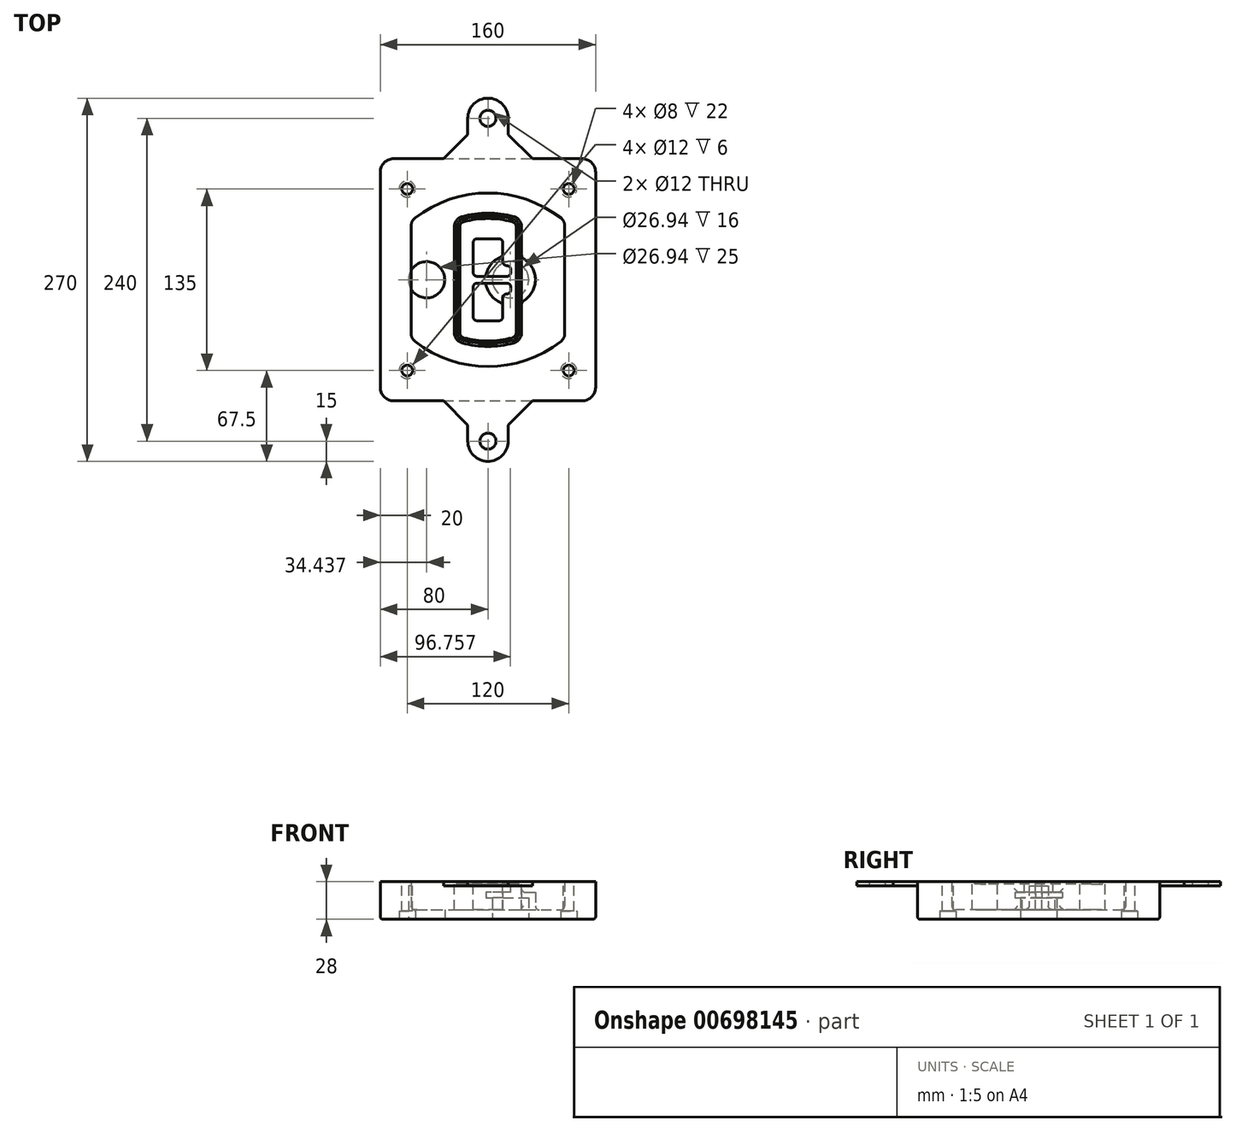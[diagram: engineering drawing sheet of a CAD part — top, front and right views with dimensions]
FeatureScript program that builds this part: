
annotation { "Feature Type Name" : "Feature", "Feature Type Description" : "" }
export const myFeature = defineFeature(function(context is Context, id is Id, definition is map)
    precondition{}
    {
        {
            var Q0;
            Q0=qCreatedBy(makeId("Top.planeOp"),FACE);
            var sketch = newSketch(context, id + "F0", { "sketchPlane" : qUnion([Q0])});
            skPoint(sketch, "E0.rect.middle", {"position": v(0, 0) * mm});
            skLineSegment(sketch, "E1.bottom", {"start": v(-70, -90) * mm, "end": v(70, -90) * mm});
            skLineSegment(sketch, "E1.top", {"start": v(-70, 90) * mm, "end": v(70, 90) * mm});
            skLineSegment(sketch, "E1.left", {"start": v(-80, -80) * mm, "end": v(-80, 80) * mm});
            skLineSegment(sketch, "E1.right", {"start": v(80, -80) * mm, "end": v(80, 80) * mm});
            skLineSegment(sketch, "E2", {"start": v(-80, 90) * mm, "end": v(80, -90) * mm, "construction": true});
            skLineSegment(sketch, "E3", {"start": v(80, 90) * mm, "end": v(-80, -90) * mm, "construction": true});
            skCircle(sketch, "E4", {"center": v(-60, 67.5) * mm, "radius": 4 * mm});
            skCircle(sketch, "E5", {"center": v(60, 67.5) * mm, "radius": 4 * mm});
            skCircle(sketch, "E6", {"center": v(60, -67.5) * mm, "radius": 4 * mm});
            skCircle(sketch, "E7", {"center": v(-60, -67.5) * mm, "radius": 4 * mm});
            skLineSegment(sketch, "E8", {"start": v(-60, 67.5) * mm, "end": v(60, 67.5) * mm, "construction": true});
            skLineSegment(sketch, "E9", {"start": v(60, 67.5) * mm, "end": v(60, -67.5) * mm, "construction": true});
            skLineSegment(sketch, "E10", {"start": v(60, -67.5) * mm, "end": v(-60, -67.5) * mm, "construction": true});
            skLineSegment(sketch, "E11", {"start": v(-60, -67.5) * mm, "end": v(-60, 67.5) * mm, "construction": true});
            skLineSegment(sketch, "E12", {"start": v(-60, 40.3) * mm, "end": v(-60, -40.3) * mm});
            skLineSegment(sketch, "E13", {"start": v(60, 40.3) * mm, "end": v(60, -40.3) * mm});
            skArc(sketch, "E14", {"start": v(56.15, 48.18) * mm, "mid": v(0, 67.5) * mm, "end": v(-56.15, 48.18) * mm});
            skArc(sketch, "E15", {"start": v(-56.15, -48.18) * mm, "mid": v(0, -67.5) * mm, "end": v(56.15, -48.18) * mm});
            skLineSegment(sketch, "E16", {"start": v(-60, 0) * mm, "end": v(60, 0) * mm, "construction": true});
            skPoint(sketch, "E17.visualSharp", {"position": v(-60, -45) * mm});
            skArc(sketch, "E17.filletArc", {"start": v(-60, -40.3) * mm, "mid": v(-58.99, -44.68) * mm, "end": v(-56.15, -48.18) * mm});
            skPoint(sketch, "E18.visualSharp", {"position": v(-60, 45) * mm});
            skArc(sketch, "E18.filletArc", {"start": v(-56.15, 48.18) * mm, "mid": v(-58.99, 44.68) * mm, "end": v(-60, 40.3) * mm});
            skPoint(sketch, "E19.visualSharp", {"position": v(60, 45) * mm});
            skArc(sketch, "E19.filletArc", {"start": v(60, 40.3) * mm, "mid": v(58.99, 44.68) * mm, "end": v(56.15, 48.18) * mm});
            skPoint(sketch, "E20.visualSharp", {"position": v(60, -45) * mm});
            skArc(sketch, "E20.filletArc", {"start": v(56.15, -48.18) * mm, "mid": v(58.99, -44.68) * mm, "end": v(60, -40.3) * mm});
            skPoint(sketch, "E21.visualSharp", {"position": v(-80, 90) * mm});
            skArc(sketch, "E21.filletArc", {"start": v(-70, 90) * mm, "mid": v(-77.07, 87.07) * mm, "end": v(-80, 80) * mm});
            skPoint(sketch, "E22.visualSharp", {"position": v(80, 90) * mm});
            skArc(sketch, "E22.filletArc", {"start": v(80, 80) * mm, "mid": v(77.07, 87.07) * mm, "end": v(70, 90) * mm});
            skPoint(sketch, "E23.visualSharp", {"position": v(80, -90) * mm});
            skArc(sketch, "E23.filletArc", {"start": v(70, -90) * mm, "mid": v(77.07, -87.07) * mm, "end": v(80, -80) * mm});
            skPoint(sketch, "E24.visualSharp", {"position": v(-80, -90) * mm});
            skArc(sketch, "E24.filletArc", {"start": v(-80, -80) * mm, "mid": v(-77.07, -87.07) * mm, "end": v(-70, -90) * mm});
            skArc(sketch, "E25.0", {"start": v(57, 40.3) * mm, "mid": v(56.3, 43.36) * mm, "end": v(54.3, 45.81) * mm});
            skLineSegment(sketch, "E25.1", {"start": v(57, 40.3) * mm, "end": v(57, -40.3) * mm});
            skArc(sketch, "E25.2", {"start": v(54.3, -45.81) * mm, "mid": v(56.3, -43.36) * mm, "end": v(57, -40.3) * mm});
            skArc(sketch, "E25.3", {"start": v(-54.3, -45.81) * mm, "mid": v(0, -64.5) * mm, "end": v(54.3, -45.81) * mm});
            skArc(sketch, "E25.4", {"start": v(-57, -40.3) * mm, "mid": v(-56.3, -43.36) * mm, "end": v(-54.3, -45.81) * mm});
            skArc(sketch, "E25.5", {"start": v(54.3, 45.81) * mm, "mid": v(0, 64.5) * mm, "end": v(-54.3, 45.81) * mm});
            skLineSegment(sketch, "E25.6", {"start": v(-57, 40.3) * mm, "end": v(-57, -40.3) * mm});
            skArc(sketch, "E25.7", {"start": v(-54.3, 45.81) * mm, "mid": v(-56.3, 43.36) * mm, "end": v(-57, 40.3) * mm});
            skArc(sketch, "E26.0", {"start": v(-58.62, 51.33) * mm, "mid": v(-62.58, 46.43) * mm, "end": v(-64, 40.3) * mm});
            skArc(sketch, "E26.1", {"start": v(58.62, 51.33) * mm, "mid": v(0, 71.5) * mm, "end": v(-58.62, 51.33) * mm});
            skArc(sketch, "E26.2", {"start": v(64, 40.3) * mm, "mid": v(62.58, 46.43) * mm, "end": v(58.62, 51.33) * mm});
            skLineSegment(sketch, "E26.3", {"start": v(64, 40.3) * mm, "end": v(64, -40.3) * mm});
            skArc(sketch, "E26.4", {"start": v(58.62, -51.33) * mm, "mid": v(62.58, -46.43) * mm, "end": v(64, -40.3) * mm});
            skLineSegment(sketch, "E26.5", {"start": v(-64, 40.3) * mm, "end": v(-64, -40.3) * mm});
            skArc(sketch, "E26.6", {"start": v(-58.62, -51.33) * mm, "mid": v(0, -71.5) * mm, "end": v(58.62, -51.33) * mm});
            skArc(sketch, "E26.7", {"start": v(-64, -40.3) * mm, "mid": v(-62.58, -46.43) * mm, "end": v(-58.62, -51.33) * mm});
            skSolve(sketch);
        }
        {
            var Q0;
            Q0=makeQuery(id+"F0.imprint","IMPRINT",FACE,{"disambiguationData":[TD([[makeQuery(id+"F0.imprint","IMPRINT",EDGE,{"derivedFrom":sQuery(id+"F0.wireOp",EDGE,"E1.bottom")}),1.0]])]});
            var Q1;
            Q1=makeQuery(id+"F0.imprint","IMPRINT",FACE,{"disambiguationData":[TD([[makeQuery(id+"F0.imprint","IMPRINT",EDGE,{"derivedFrom":sQuery(id+"F0.wireOp",EDGE,"E12")}),1.0]])]});
            var Q2;
            Q2=makeQuery(id+"F0.imprint","IMPRINT",FACE,{"disambiguationData":[TD([[makeQuery(id+"F0.imprint","IMPRINT",EDGE,{"derivedFrom":sQuery(id+"F0.wireOp",EDGE,"E25.0")}),1.0]])]});
            var Q3;
            Q3=makeQuery(id+"F0.imprint","IMPRINT",FACE,{"disambiguationData":[TD([[makeQuery(id+"F0.imprint","IMPRINT",EDGE,{"derivedFrom":sQuery(id+"F0.wireOp",EDGE,"E12")}),-1.0]])]});
            extrude(context, id + "F1", {"entities" : qUnion([Q0, Q1, Q2, Q3]), "oppositeDirection" : true, "depth" : 25 * mm});
        }
        {
            var Q0;
            Q0=makeQuery(id+"F0.imprint","IMPRINT",FACE,{"disambiguationData":[TD([[makeQuery(id+"F0.imprint","IMPRINT",EDGE,{"derivedFrom":sQuery(id+"F0.wireOp",EDGE,"E12")}),1.0]])]});
            extrude(context, id + "F2", {"entities" : qUnion([Q0]), "operationType" : NewBodyOperationType.ADD, "depth" : 3 * mm});
        }
        {
            var Q0;
            Q0=makeQuery(id+"F0.imprint","IMPRINT",FACE,{"disambiguationData":[TD([[makeQuery(id+"F0.imprint","IMPRINT",EDGE,{"derivedFrom":sQuery(id+"F0.wireOp",EDGE,"E25.0")}),1.0]])]});
            extrude(context, id + "F3", {"entities" : qUnion([Q0]), "operationType" : NewBodyOperationType.REMOVE, "oppositeDirection" : true, "depth" : 18 * mm});
        }
        {
            var Q0;
            Q0=makeQuery(id+"F2.opExtrude","CAP_FACE",FACE,{"disambiguationData":[OSD([sQuery(id+"F0.wireOp",EDGE,"E12"),sQuery(id+"F0.wireOp",EDGE,"E13"),sQuery(id+"F0.wireOp",EDGE,"E14"),sQuery(id+"F0.wireOp",EDGE,"E15"),sQuery(id+"F0.wireOp",EDGE,"E17.filletArc"),sQuery(id+"F0.wireOp",EDGE,"E18.filletArc"),sQuery(id+"F0.wireOp",EDGE,"E19.filletArc"),sQuery(id+"F0.wireOp",EDGE,"E20.filletArc"),sQuery(id+"F0.wireOp",EDGE,"E25.0"),sQuery(id+"F0.wireOp",EDGE,"E25.1"),sQuery(id+"F0.wireOp",EDGE,"E25.2"),sQuery(id+"F0.wireOp",EDGE,"E25.3"),sQuery(id+"F0.wireOp",EDGE,"E25.4"),sQuery(id+"F0.wireOp",EDGE,"E25.5"),sQuery(id+"F0.wireOp",EDGE,"E25.6"),sQuery(id+"F0.wireOp",EDGE,"E25.7")])],"isStart":false});
            var sketch = newSketch(context, id + "F4", { "sketchPlane" : qUnion([Q0])});
            skArc(sketch, "E27.0", {"start": v(-19.08, -46.97) * mm, "mid": v(0, -49.5) * mm, "end": v(19.08, -46.97) * mm});
            skArc(sketch, "E28.0", {"start": v(19.08, 46.97) * mm, "mid": v(0, 49.5) * mm, "end": v(-19.08, 46.97) * mm});
            skLineSegment(sketch, "E29", {"start": v(-25, 39.25) * mm, "end": v(-25, -39.25) * mm});
            skLineSegment(sketch, "E30", {"start": v(25, 39.25) * mm, "end": v(25, -39.25) * mm});
            skLineSegment(sketch, "E31", {"start": v(-25, 45.1) * mm, "end": v(25, 45.1) * mm, "construction": true});
            skLineSegment(sketch, "E32", {"start": v(-25, -45.1) * mm, "end": v(25, -45.1) * mm, "construction": true});
            skPoint(sketch, "E33.visualSharp", {"position": v(-25, 45.1) * mm});
            skArc(sketch, "E33.filletArc", {"start": v(-19.08, 46.97) * mm, "mid": v(-23.35, 44.11) * mm, "end": v(-25, 39.25) * mm});
            skPoint(sketch, "E34.visualSharp", {"position": v(25, 45.1) * mm});
            skArc(sketch, "E34.filletArc", {"start": v(25, 39.25) * mm, "mid": v(23.35, 44.11) * mm, "end": v(19.08, 46.97) * mm});
            skPoint(sketch, "E35.visualSharp", {"position": v(25, -45.1) * mm});
            skArc(sketch, "E35.filletArc", {"start": v(19.08, -46.97) * mm, "mid": v(23.35, -44.11) * mm, "end": v(25, -39.25) * mm});
            skPoint(sketch, "E36.visualSharp", {"position": v(-25, -45.1) * mm});
            skArc(sketch, "E36.filletArc", {"start": v(-25, -39.25) * mm, "mid": v(-23.35, -44.11) * mm, "end": v(-19.08, -46.97) * mm});
            skArc(sketch, "E37.0", {"start": v(54.3, 45.81) * mm, "mid": v(0, 64.5) * mm, "end": v(-54.3, 45.81) * mm});
            skArc(sketch, "E37.1", {"start": v(-54.3, 45.81) * mm, "mid": v(-56.3, 43.36) * mm, "end": v(-57, 40.3) * mm});
            skLineSegment(sketch, "E37.2", {"start": v(-57, 40.3) * mm, "end": v(-57, -40.3) * mm});
            skArc(sketch, "E37.3", {"start": v(-57, -40.3) * mm, "mid": v(-56.3, -43.36) * mm, "end": v(-54.3, -45.81) * mm});
            skArc(sketch, "E37.4", {"start": v(-54.3, -45.81) * mm, "mid": v(0, -64.5) * mm, "end": v(54.3, -45.81) * mm});
            skArc(sketch, "E37.5", {"start": v(54.3, -45.81) * mm, "mid": v(56.3, -43.36) * mm, "end": v(57, -40.3) * mm});
            skLineSegment(sketch, "E37.6", {"start": v(57, 40.3) * mm, "end": v(57, -40.3) * mm});
            skArc(sketch, "E37.7", {"start": v(57, 40.3) * mm, "mid": v(56.3, 43.36) * mm, "end": v(54.3, 45.81) * mm});
            skLineSegment(sketch, "E38.0", {"start": v(23, 39.25) * mm, "end": v(23, -39.25) * mm});
            skArc(sketch, "E38.1", {"start": v(18.56, -45.04) * mm, "mid": v(21.76, -42.9) * mm, "end": v(23, -39.25) * mm});
            skArc(sketch, "E38.2", {"start": v(-18.56, -45.04) * mm, "mid": v(0, -47.5) * mm, "end": v(18.56, -45.04) * mm});
            skArc(sketch, "E38.3", {"start": v(-23, -39.25) * mm, "mid": v(-21.76, -42.9) * mm, "end": v(-18.56, -45.04) * mm});
            skLineSegment(sketch, "E38.4", {"start": v(-23, 39.25) * mm, "end": v(-23, -39.25) * mm});
            skArc(sketch, "E38.5", {"start": v(23, 39.25) * mm, "mid": v(21.76, 42.9) * mm, "end": v(18.56, 45.04) * mm});
            skArc(sketch, "E38.6", {"start": v(-18.56, 45.04) * mm, "mid": v(-21.76, 42.9) * mm, "end": v(-23, 39.25) * mm});
            skArc(sketch, "E38.7", {"start": v(18.56, 45.04) * mm, "mid": v(0, 47.5) * mm, "end": v(-18.56, 45.04) * mm});
            skArc(sketch, "E39.0", {"start": v(21, 39.25) * mm, "mid": v(20.18, 41.68) * mm, "end": v(18.04, 43.1) * mm});
            skLineSegment(sketch, "E39.1", {"start": v(21, 39.25) * mm, "end": v(21, -39.25) * mm});
            skArc(sketch, "E39.2", {"start": v(18.04, -43.1) * mm, "mid": v(20.18, -41.68) * mm, "end": v(21, -39.25) * mm});
            skArc(sketch, "E39.3", {"start": v(-18.04, -43.1) * mm, "mid": v(0, -45.5) * mm, "end": v(18.04, -43.1) * mm});
            skArc(sketch, "E39.4", {"start": v(-21, -39.25) * mm, "mid": v(-20.18, -41.68) * mm, "end": v(-18.04, -43.1) * mm});
            skArc(sketch, "E39.5", {"start": v(18.04, 43.1) * mm, "mid": v(0, 45.5) * mm, "end": v(-18.04, 43.1) * mm});
            skLineSegment(sketch, "E39.6", {"start": v(-21, 39.25) * mm, "end": v(-21, -39.25) * mm});
            skArc(sketch, "E39.7", {"start": v(-18.04, 43.1) * mm, "mid": v(-20.18, 41.68) * mm, "end": v(-21, 39.25) * mm});
            skLineSegment(sketch, "E40", {"start": v(-25, 0) * mm, "end": v(25, 0) * mm, "construction": true});
            skLineSegment(sketch, "E41", {"start": v(-11, 5.5) * mm, "end": v(-11, 27.5) * mm});
            skLineSegment(sketch, "E42", {"start": v(-8, 30.5) * mm, "end": v(8, 30.5) * mm});
            skLineSegment(sketch, "E43", {"start": v(11, 27.5) * mm, "end": v(11, 13.5) * mm});
            skLineSegment(sketch, "E44", {"start": v(14, 10.5) * mm, "end": v(14, 10.5) * mm});
            skLineSegment(sketch, "E45", {"start": v(17, 7.5) * mm, "end": v(17, 5.5) * mm});
            skLineSegment(sketch, "E46", {"start": v(14, 2.5) * mm, "end": v(-8, 2.5) * mm});
            skPoint(sketch, "E47.visualSharp", {"position": v(-11, 30.5) * mm});
            skArc(sketch, "E47.filletArc", {"start": v(-8, 30.5) * mm, "mid": v(-10.12, 29.62) * mm, "end": v(-11, 27.5) * mm});
            skPoint(sketch, "E48.visualSharp", {"position": v(11, 30.5) * mm});
            skArc(sketch, "E48.filletArc", {"start": v(11, 27.5) * mm, "mid": v(10.12, 29.62) * mm, "end": v(8, 30.5) * mm});
            skPoint(sketch, "E49.visualSharp", {"position": v(11, 10.5) * mm});
            skArc(sketch, "E49.filletArc", {"start": v(11, 13.5) * mm, "mid": v(11.88, 11.38) * mm, "end": v(14, 10.5) * mm});
            skPoint(sketch, "E50.visualSharp", {"position": v(17, 10.5) * mm});
            skArc(sketch, "E50.filletArc", {"start": v(17, 7.5) * mm, "mid": v(16.12, 9.62) * mm, "end": v(14, 10.5) * mm});
            skPoint(sketch, "E51.visualSharp", {"position": v(17, 2.5) * mm});
            skArc(sketch, "E51.filletArc", {"start": v(14, 2.5) * mm, "mid": v(16.12, 3.38) * mm, "end": v(17, 5.5) * mm});
            skPoint(sketch, "E52.visualSharp", {"position": v(-11, 2.5) * mm});
            skArc(sketch, "E52.filletArc", {"start": v(-11, 5.5) * mm, "mid": v(-10.12, 3.38) * mm, "end": v(-8, 2.5) * mm});
            skLineSegment(sketch, "E53.0.MirrorCS", {"start": v(14, -2.5) * mm, "end": v(-8, -2.5) * mm});
            skArc(sketch, "E54.0.MirrorCS", {"start": v(-11, -5.5) * mm, "mid": v(-10.12, -3.38) * mm, "end": v(-8, -2.5) * mm});
            skLineSegment(sketch, "E55.0.MirrorCS", {"start": v(-11, -5.5) * mm, "end": v(-11, -27.5) * mm});
            skArc(sketch, "E56.0.MirrorCS", {"start": v(-8, -30.5) * mm, "mid": v(-10.12, -29.62) * mm, "end": v(-11, -27.5) * mm});
            skLineSegment(sketch, "E57.0.MirrorCS", {"start": v(-8, -30.5) * mm, "end": v(8, -30.5) * mm});
            skArc(sketch, "E58.0.MirrorCS", {"start": v(11, -27.5) * mm, "mid": v(10.12, -29.62) * mm, "end": v(8, -30.5) * mm});
            skLineSegment(sketch, "E59.0.MirrorCS", {"start": v(11, -27.5) * mm, "end": v(11, -13.5) * mm});
            skArc(sketch, "E60.0.MirrorCS", {"start": v(11, -13.5) * mm, "mid": v(11.88, -11.38) * mm, "end": v(14, -10.5) * mm});
            skArc(sketch, "E61.0.MirrorCS", {"start": v(17, -7.5) * mm, "mid": v(16.12, -9.62) * mm, "end": v(14, -10.5) * mm});
            skLineSegment(sketch, "E62.0.MirrorCS", {"start": v(17, -7.5) * mm, "end": v(17, -5.5) * mm});
            skArc(sketch, "E63.0.MirrorCS", {"start": v(14, -2.5) * mm, "mid": v(16.12, -3.38) * mm, "end": v(17, -5.5) * mm});
            skSolve(sketch);
        }
        {
            var Q0;
            Q0=makeQuery(id+"F4.imprint","IMPRINT",FACE,{"disambiguationData":[TD([[makeQuery(id+"F4.imprint","IMPRINT",EDGE,{"derivedFrom":sQuery(id+"F4.wireOp",EDGE,"E27.0")}),1.0]])]});
            var Q1;
            Q1=makeQuery(id+"F4.imprint","IMPRINT",FACE,{"disambiguationData":[TD([[makeQuery(id+"F4.imprint","IMPRINT",EDGE,{"derivedFrom":sQuery(id+"F4.wireOp",EDGE,"E38.0")}),-1.0]])]});
            var Q2;
            Q2=makeQuery(id+"F4.imprint","IMPRINT",FACE,{"disambiguationData":[TD([[makeQuery(id+"F4.imprint","IMPRINT",EDGE,{"derivedFrom":sQuery(id+"F4.wireOp",EDGE,"E39.0")}),1.0]])]});
            extrude(context, id + "F5", {"entities" : qUnion([Q0, Q1, Q2]), "operationType" : NewBodyOperationType.ADD, "endBound" : BoundingType.UP_TO_NEXT, "oppositeDirection" : true, "depth" : 25 * mm});
        }
        {
            var Q0;
            Q0=makeQuery(id+"F4.imprint","IMPRINT",FACE,{"disambiguationData":[TD([[makeQuery(id+"F4.imprint","IMPRINT",EDGE,{"derivedFrom":sQuery(id+"F4.wireOp",EDGE,"E38.0")}),-1.0]])]});
            extrude(context, id + "F6", {"entities" : qUnion([Q0]), "operationType" : NewBodyOperationType.REMOVE, "oppositeDirection" : true, "depth" : 2 * mm});
        }
        {
            var Q0;
            Q0=makeQuery(id+"F1.opExtrude","CAP_FACE",FACE,{"disambiguationData":[OSD([sQuery(id+"F0.wireOp",EDGE,"E1.bottom"),sQuery(id+"F0.wireOp",EDGE,"E1.top"),sQuery(id+"F0.wireOp",EDGE,"E1.left"),sQuery(id+"F0.wireOp",EDGE,"E1.right"),sQuery(id+"F0.wireOp",EDGE,"E4"),sQuery(id+"F0.wireOp",EDGE,"E5"),sQuery(id+"F0.wireOp",EDGE,"E6"),sQuery(id+"F0.wireOp",EDGE,"E7"),sQuery(id+"F0.wireOp",EDGE,"E21.filletArc"),sQuery(id+"F0.wireOp",EDGE,"E22.filletArc"),sQuery(id+"F0.wireOp",EDGE,"E23.filletArc"),sQuery(id+"F0.wireOp",EDGE,"E24.filletArc")])],"isStart":false});
            var sketch = newSketch(context, id + "F7", { "sketchPlane" : qUnion([Q0])});
            skCircle(sketch, "E64", {"center": v(16.76, 0) * mm, "radius": 13.47 * mm});
            skCircle(sketch, "E65", {"center": v(-45.56, 0) * mm, "radius": 13.47 * mm});
            skLineSegment(sketch, "E66", {"start": v(80, 0) * mm, "end": v(-80, 0) * mm});
            skCircle(sketch, "E67", {"center": v(16.76, 0) * mm, "radius": 18.47 * mm});
            skCircle(sketch, "E68", {"center": v(60, -67.5) * mm, "radius": 6 * mm});
            skCircle(sketch, "E69", {"center": v(-60, -67.5) * mm, "radius": 6 * mm});
            skCircle(sketch, "E70", {"center": v(-60, 67.5) * mm, "radius": 6 * mm});
            skCircle(sketch, "E71", {"center": v(60, 67.5) * mm, "radius": 6 * mm});
            skSolve(sketch);
        }
        {
            var Q0;
            {var subQ1=sQuery(id+"F7.wireOp",EDGE,"E66");var subQ4=sQuery(id+"F7.wireOp",EDGE,"E64");var subQ6=makeQuery(id+"F7.imprint","INTERSECT",VERTEX,{"disambiguationData":[OD(0.0)],"derivedFrom":[subQ4,subQ1]});Q0=makeQuery(id+"F7.imprint","IMPRINT",FACE,{"disambiguationData":[TD([[makeQuery(id+"F7.imprint","IMPRINT",EDGE,{"disambiguationData":[TD([[subQ6,-1.0]])],"derivedFrom":subQ4}),-1.0]])]});}
            var Q1;
            {var subQ0=sQuery(id+"F7.wireOp",EDGE,"E66");var subQ1=sQuery(id+"F7.wireOp",EDGE,"E64");var subQ3=makeQuery(id+"F7.imprint","INTERSECT",VERTEX,{"disambiguationData":[OD(0.0)],"derivedFrom":[subQ1,subQ0]});Q1=makeQuery(id+"F7.imprint","IMPRINT",FACE,{"disambiguationData":[TD([[makeQuery(id+"F7.imprint","IMPRINT",EDGE,{"disambiguationData":[TD([[subQ3,-1.0]])],"derivedFrom":subQ1}),1.0]])]});}
            var Q2;
            {var subQ0=sQuery(id+"F7.wireOp",EDGE,"E66");var subQ1=sQuery(id+"F7.wireOp",EDGE,"E64");var subQ3=makeQuery(id+"F7.imprint","INTERSECT",VERTEX,{"disambiguationData":[OD(0.0)],"derivedFrom":[subQ1,subQ0]});Q2=makeQuery(id+"F7.imprint","IMPRINT",FACE,{"disambiguationData":[TD([[makeQuery(id+"F7.imprint","IMPRINT",EDGE,{"disambiguationData":[TD([[subQ3,1.0]])],"derivedFrom":subQ1}),1.0]])]});}
            var Q3;
            {var subQ1=sQuery(id+"F7.wireOp",EDGE,"E66");var subQ4=sQuery(id+"F7.wireOp",EDGE,"E64");var subQ6=makeQuery(id+"F7.imprint","INTERSECT",VERTEX,{"disambiguationData":[OD(0.0)],"derivedFrom":[subQ4,subQ1]});Q3=makeQuery(id+"F7.imprint","IMPRINT",FACE,{"disambiguationData":[TD([[makeQuery(id+"F7.imprint","IMPRINT",EDGE,{"disambiguationData":[TD([[subQ6,1.0]])],"derivedFrom":subQ4}),-1.0]])]});}
            extrude(context, id + "F8", {"entities" : qUnion([Q0, Q1, Q2, Q3]), "operationType" : NewBodyOperationType.ADD, "oppositeDirection" : true, "depth" : 20 * mm});
        }
        {
            var Q0;
            {var subQ0=sQuery(id+"F7.wireOp",EDGE,"E66");var subQ1=sQuery(id+"F7.wireOp",EDGE,"E64");var subQ3=makeQuery(id+"F7.imprint","INTERSECT",VERTEX,{"disambiguationData":[OD(0.0)],"derivedFrom":[subQ1,subQ0]});Q0=makeQuery(id+"F7.imprint","IMPRINT",FACE,{"disambiguationData":[TD([[makeQuery(id+"F7.imprint","IMPRINT",EDGE,{"disambiguationData":[TD([[subQ3,-1.0]])],"derivedFrom":subQ1}),1.0]])]});}
            var Q1;
            {var subQ0=sQuery(id+"F7.wireOp",EDGE,"E66");var subQ1=sQuery(id+"F7.wireOp",EDGE,"E64");var subQ3=makeQuery(id+"F7.imprint","INTERSECT",VERTEX,{"disambiguationData":[OD(0.0)],"derivedFrom":[subQ1,subQ0]});Q1=makeQuery(id+"F7.imprint","IMPRINT",FACE,{"disambiguationData":[TD([[makeQuery(id+"F7.imprint","IMPRINT",EDGE,{"disambiguationData":[TD([[subQ3,1.0]])],"derivedFrom":subQ1}),1.0]])]});}
            extrude(context, id + "F9", {"entities" : qUnion([Q0, Q1]), "operationType" : NewBodyOperationType.REMOVE, "oppositeDirection" : true, "depth" : 16 * mm});
        }
        {
            var Q0;
            {var subQ0=sQuery(id+"F7.wireOp",EDGE,"E66");var subQ1=sQuery(id+"F7.wireOp",EDGE,"E65");var subQ3=makeQuery(id+"F7.imprint","INTERSECT",VERTEX,{"disambiguationData":[OD(0.0)],"derivedFrom":[subQ1,subQ0]});Q0=makeQuery(id+"F7.imprint","IMPRINT",FACE,{"disambiguationData":[TD([[makeQuery(id+"F7.imprint","IMPRINT",EDGE,{"disambiguationData":[TD([[subQ3,-1.0]])],"derivedFrom":subQ1}),1.0]])]});}
            var Q1;
            {var subQ0=sQuery(id+"F7.wireOp",EDGE,"E66");var subQ1=sQuery(id+"F7.wireOp",EDGE,"E65");var subQ3=makeQuery(id+"F7.imprint","INTERSECT",VERTEX,{"disambiguationData":[OD(0.0)],"derivedFrom":[subQ1,subQ0]});Q1=makeQuery(id+"F7.imprint","IMPRINT",FACE,{"disambiguationData":[TD([[makeQuery(id+"F7.imprint","IMPRINT",EDGE,{"disambiguationData":[TD([[subQ3,1.0]])],"derivedFrom":subQ1}),1.0]])]});}
            extrude(context, id + "F10", {"entities" : qUnion([Q0, Q1]), "operationType" : NewBodyOperationType.REMOVE, "oppositeDirection" : true, "depth" : 25 * mm});
        }
        {
            var Q0;
            Q0=makeQuery(id+"F7.imprint","IMPRINT",FACE,{"disambiguationData":[TD([[makeQuery(id+"F7.imprint","IMPRINT",EDGE,{"derivedFrom":sQuery(id+"F7.wireOp",EDGE,"E68")}),1.0]])]});
            var Q1;
            Q1=makeQuery(id+"F7.imprint","IMPRINT",FACE,{"disambiguationData":[TD([[makeQuery(id+"F7.imprint","IMPRINT",EDGE,{"derivedFrom":makeQuery(id+"F1.opExtrude","CAP_EDGE",EDGE,{"disambiguationData":[OSD([sQuery(id+"F0.wireOp",EDGE,"E5")])],"isStart":false})}),-1.0]])]});
            var Q2;
            Q2=makeQuery(id+"F7.imprint","IMPRINT",FACE,{"disambiguationData":[TD([[makeQuery(id+"F7.imprint","IMPRINT",EDGE,{"derivedFrom":sQuery(id+"F7.wireOp",EDGE,"E69")}),1.0]])]});
            var Q3;
            Q3=makeQuery(id+"F7.imprint","IMPRINT",FACE,{"disambiguationData":[TD([[makeQuery(id+"F7.imprint","IMPRINT",EDGE,{"derivedFrom":makeQuery(id+"F1.opExtrude","CAP_EDGE",EDGE,{"disambiguationData":[OSD([sQuery(id+"F0.wireOp",EDGE,"E4")])],"isStart":false})}),-1.0]])]});
            var Q4;
            Q4=makeQuery(id+"F7.imprint","IMPRINT",FACE,{"disambiguationData":[TD([[makeQuery(id+"F7.imprint","IMPRINT",EDGE,{"derivedFrom":sQuery(id+"F7.wireOp",EDGE,"E70")}),1.0]])]});
            var Q5;
            Q5=makeQuery(id+"F7.imprint","IMPRINT",FACE,{"disambiguationData":[TD([[makeQuery(id+"F7.imprint","IMPRINT",EDGE,{"derivedFrom":makeQuery(id+"F1.opExtrude","CAP_EDGE",EDGE,{"disambiguationData":[OSD([sQuery(id+"F0.wireOp",EDGE,"E7")])],"isStart":false})}),-1.0]])]});
            var Q6;
            Q6=makeQuery(id+"F7.imprint","IMPRINT",FACE,{"disambiguationData":[TD([[makeQuery(id+"F7.imprint","IMPRINT",EDGE,{"derivedFrom":sQuery(id+"F7.wireOp",EDGE,"E71")}),1.0]])]});
            var Q7;
            Q7=makeQuery(id+"F7.imprint","IMPRINT",FACE,{"disambiguationData":[TD([[makeQuery(id+"F7.imprint","IMPRINT",EDGE,{"derivedFrom":makeQuery(id+"F1.opExtrude","CAP_EDGE",EDGE,{"disambiguationData":[OSD([sQuery(id+"F0.wireOp",EDGE,"E6")])],"isStart":false})}),-1.0]])]});
            extrude(context, id + "F11", {"entities" : qUnion([Q0, Q1, Q2, Q3, Q4, Q5, Q6, Q7]), "operationType" : NewBodyOperationType.REMOVE, "oppositeDirection" : true, "depth" : 6 * mm});
        }
        {
            var Q0;
            Q0=makeQuery(id+"F9.boolean.opBoolean","COPY",FACE,{"derivedFrom":makeQuery(id+"F9.opExtrude","CAP_FACE",FACE,{"disambiguationData":[OSD([sQuery(id+"F7.wireOp",EDGE,"E64")])],"isStart":false})});
            var sketch = newSketch(context, id + "F12", { "sketchPlane" : qUnion([Q0])});
            skArc(sketch, "E72.0", {"start": v(11, 17.55) * mm, "mid": v(2.57, 11.82) * mm, "end": v(-1.54, 2.5) * mm});
            skArc(sketch, "E72.1", {"start": v(-1.54, -2.5) * mm, "mid": v(2.57, -11.82) * mm, "end": v(11, -17.55) * mm});
            skLineSegment(sketch, "E73", {"start": v(-1.54, -2.5) * mm, "end": v(14, -2.5) * mm});
            skLineSegment(sketch, "E74.0", {"start": v(14, 2.5) * mm, "end": v(-1.54, 2.5) * mm});
            skArc(sketch, "E74.1", {"start": v(14, 2.5) * mm, "mid": v(16.12, 3.38) * mm, "end": v(17, 5.5) * mm});
            skLineSegment(sketch, "E74.2", {"start": v(17, 7.5) * mm, "end": v(17, 5.5) * mm});
            skArc(sketch, "E74.3", {"start": v(17, 7.5) * mm, "mid": v(16.12, 9.62) * mm, "end": v(14, 10.5) * mm});
            skArc(sketch, "E74.4", {"start": v(11, 13.5) * mm, "mid": v(11.88, 11.38) * mm, "end": v(14, 10.5) * mm});
            skLineSegment(sketch, "E74.5", {"start": v(11, 17.55) * mm, "end": v(11, 13.5) * mm});
            skLineSegment(sketch, "E74.7", {"start": v(14, -2.5) * mm, "end": v(-1.54, -2.5) * mm});
            skArc(sketch, "E74.8", {"start": v(14, -2.5) * mm, "mid": v(16.12, -3.38) * mm, "end": v(17, -5.5) * mm});
            skLineSegment(sketch, "E74.9", {"start": v(17, -7.5) * mm, "end": v(17, -5.5) * mm});
            skArc(sketch, "E74.10", {"start": v(17, -7.5) * mm, "mid": v(16.12, -9.62) * mm, "end": v(14, -10.5) * mm});
            skArc(sketch, "E74.11", {"start": v(11, -13.5) * mm, "mid": v(11.88, -11.38) * mm, "end": v(14, -10.5) * mm});
            skLineSegment(sketch, "E74.12", {"start": v(11, -17.55) * mm, "end": v(11, -13.5) * mm});
            skPoint(sketch, "E75.orphan", {"position": v(11, -27.5) * mm});
            skPoint(sketch, "E76.orphan", {"position": v(-8, -2.5) * mm});
            skPoint(sketch, "E77.orphan", {"position": v(-8, 2.5) * mm});
            skPoint(sketch, "E78.orphan", {"position": v(11, 27.5) * mm});
            skSolve(sketch);
        }
        {
            var Q0;
            {var subQ7=sQuery(id+"F12.wireOp",EDGE,"E72.0");var subQ14=sQuery(id+"F12.wireOp",EDGE,"E72.1");var subQ16=sQuery(id+"F12.wireOp",EDGE,"E74.1");var subQ18=sQuery(id+"F12.wireOp",EDGE,"E74.8");Q0=qUnion([makeQuery(id+"F12.imprint","IMPRINT",FACE,{"disambiguationData":[TD([[makeQuery(id+"F12.imprint","IMPRINT",EDGE,{"derivedFrom":subQ7}),1.0]])]}),makeQuery(id+"F12.imprint","IMPRINT",FACE,{"disambiguationData":[TD([[makeQuery(id+"F12.imprint","IMPRINT",EDGE,{"derivedFrom":subQ14}),1.0]])]}),makeQuery(id+"F12.imprint","IMPRINT",FACE,{"disambiguationData":[TD([[makeQuery(id+"F12.imprint","IMPRINT",EDGE,{"derivedFrom":subQ16}),1.0]])]}),makeQuery(id+"F12.imprint","IMPRINT",FACE,{"disambiguationData":[TD([[makeQuery(id+"F12.imprint","IMPRINT",EDGE,{"derivedFrom":subQ18}),-1.0]])]})]);}
            var Q1;
            Q1=makeQuery(id+"F5.boolean.opBoolean","SPLIT",FACE,{"disambiguationData":[TD([makeQuery(id+"F5.opExtrude","SWEPT_FACE",FACE,{"disambiguationData":[OSD([sQuery(id+"F4.wireOp",EDGE,"E41")])]})])],"derivedFrom":makeQuery(id+"F3.boolean.opBoolean","COPY",FACE,{"derivedFrom":makeQuery(id+"F3.opExtrude","CAP_FACE",FACE,{"disambiguationData":[OSD([sQuery(id+"F0.wireOp",EDGE,"E25.0"),sQuery(id+"F0.wireOp",EDGE,"E25.1"),sQuery(id+"F0.wireOp",EDGE,"E25.2"),sQuery(id+"F0.wireOp",EDGE,"E25.3"),sQuery(id+"F0.wireOp",EDGE,"E25.4"),sQuery(id+"F0.wireOp",EDGE,"E25.5"),sQuery(id+"F0.wireOp",EDGE,"E25.6"),sQuery(id+"F0.wireOp",EDGE,"E25.7")])],"isStart":false})})});
            extrude(context, id + "F13", {"entities" : qUnion([Q0]), "operationType" : NewBodyOperationType.REMOVE, "endBound" : BoundingType.UP_TO_SURFACE, "endBoundEntityFace" : qUnion([Q1]), "depth" : 25 * mm});
        }
        {
            var Q0;
            Q0=makeQuery(id+"F3.boolean.opBoolean","COPY",EDGE,{"derivedFrom":makeQuery(id+"F3.opExtrude","CAP_EDGE",EDGE,{"disambiguationData":[OSD([sQuery(id+"F0.wireOp",EDGE,"E25.6")])],"isStart":false})});
            var Q1;
            Q1=makeQuery(id+"F8.boolean.opBoolean","INTERSECT",EDGE,{"derivedFrom":[makeQuery(id+"F5.opExtrude","SWEPT_FACE",FACE,{"disambiguationData":[OSD([sQuery(id+"F4.wireOp",EDGE,"E30")])]}),makeQuery(id+"F8.opExtrude","CAP_FACE",FACE,{"disambiguationData":[OSD([sQuery(id+"F7.wireOp",EDGE,"E67")])],"isStart":false})]});
            var Q2;
            Q2=makeQuery(id+"F8.boolean.opBoolean","INTERSECT",EDGE,{"disambiguationData":[OD(1.0)],"derivedFrom":[makeQuery(id+"F5.opExtrude","SWEPT_FACE",FACE,{"disambiguationData":[OSD([sQuery(id+"F4.wireOp",EDGE,"E30")])]}),makeQuery(id+"F8.opExtrude","SWEPT_FACE",FACE,{"disambiguationData":[OSD([sQuery(id+"F7.wireOp",EDGE,"E67")])]})]});
            var Q3;
            {var subQ0=sQuery(id+"F4.wireOp",EDGE,"E30");Q3=makeQuery(id+"F8.boolean.opBoolean","SPLIT",EDGE,{"disambiguationData":[TD([makeQuery(id+"F5.opExtrude","SWEPT_FACE",FACE,{"disambiguationData":[OSD([sQuery(id+"F4.wireOp",EDGE,"E35.filletArc")])]})])],"derivedFrom":makeQuery(id+"F5.opExtrude","CAP_EDGE",EDGE,{"disambiguationData":[OSD([subQ0])],"isStart":false})});}
            var Q4;
            {var subQ0=sQuery(id+"F0.wireOp",EDGE,"E25.7");var subQ1=sQuery(id+"F0.wireOp",EDGE,"E25.1");var subQ2=sQuery(id+"F0.wireOp",EDGE,"E25.6");var subQ3=sQuery(id+"F0.wireOp",EDGE,"E25.5");var subQ4=sQuery(id+"F0.wireOp",EDGE,"E25.4");var subQ5=sQuery(id+"F0.wireOp",EDGE,"E25.0");var subQ6=sQuery(id+"F0.wireOp",EDGE,"E25.2");var subQ7=sQuery(id+"F0.wireOp",EDGE,"E25.3");Q4=makeQuery(id+"F8.boolean.opBoolean","INTERSECT",EDGE,{"derivedFrom":[makeQuery(id+"F5.boolean.opBoolean","SPLIT",FACE,{"disambiguationData":[TD([makeQuery(id+"F2.opExtrude","SWEPT_FACE",FACE,{"disambiguationData":[OSD([subQ5])]})])],"derivedFrom":makeQuery(id+"F3.boolean.opBoolean","COPY",FACE,{"derivedFrom":makeQuery(id+"F3.opExtrude","CAP_FACE",FACE,{"disambiguationData":[OSD([subQ5,subQ1,subQ6,subQ7,subQ4,subQ3,subQ2,subQ0])],"isStart":false})})}),makeQuery(id+"F8.opExtrude","SWEPT_FACE",FACE,{"disambiguationData":[OSD([sQuery(id+"F7.wireOp",EDGE,"E67")])]})]});}
            var Q5;
            Q5=makeQuery(id+"F8.boolean.opBoolean","INTERSECT",EDGE,{"disambiguationData":[OD(0.0)],"derivedFrom":[makeQuery(id+"F5.opExtrude","SWEPT_FACE",FACE,{"disambiguationData":[OSD([sQuery(id+"F4.wireOp",EDGE,"E30")])]}),makeQuery(id+"F8.opExtrude","SWEPT_FACE",FACE,{"disambiguationData":[OSD([sQuery(id+"F7.wireOp",EDGE,"E67")])]})]});
            fillet(context, id + "F14", {"entities" : qUnion([Q0, Q1, Q2, Q3, Q4, Q5]), "radius" : 3 * mm, "tangentPropagation" : true, "allowEdgeOverflow" : false});
        }
        {
            var Q0;
            Q0=makeQuery(id+"F1.opExtrude","CAP_EDGE",EDGE,{"disambiguationData":[OSD([sQuery(id+"F0.wireOp",EDGE,"E1.bottom")])],"isStart":false});
            fillet(context, id + "F15", {"entities" : qUnion([Q0]), "radius" : 2 * mm, "tangentPropagation" : true, "allowEdgeOverflow" : false});
        }
        {
            var Q0;
            {var subQ0=sQuery(id+"F0.wireOp",EDGE,"E21.filletArc");var subQ1=sQuery(id+"F0.wireOp",EDGE,"E7");var subQ2=sQuery(id+"F0.wireOp",EDGE,"E6");var subQ3=sQuery(id+"F0.wireOp",EDGE,"E5");var subQ4=sQuery(id+"F0.wireOp",EDGE,"E4");var subQ5=sQuery(id+"F0.wireOp",EDGE,"E22.filletArc");var subQ6=sQuery(id+"F0.wireOp",EDGE,"E1.bottom");var subQ7=sQuery(id+"F0.wireOp",EDGE,"E1.right");var subQ8=sQuery(id+"F0.wireOp",EDGE,"E1.top");var subQ9=sQuery(id+"F0.wireOp",EDGE,"E1.left");var subQ10=sQuery(id+"F0.wireOp",EDGE,"E23.filletArc");var subQ11=sQuery(id+"F0.wireOp",EDGE,"E24.filletArc");Q0=makeQuery(id+"F2.boolean.opBoolean","SPLIT",FACE,{"disambiguationData":[TD([makeQuery(id+"F1.opExtrude","SWEPT_FACE",FACE,{"disambiguationData":[OSD([subQ6])]})])],"derivedFrom":makeQuery(id+"F1.opExtrude","CAP_FACE",FACE,{"disambiguationData":[OSD([subQ6,subQ8,subQ9,subQ7,subQ4,subQ3,subQ2,subQ1,subQ0,subQ5,subQ10,subQ11])],"isStart":true})});}
            var sketch = newSketch(context, id + "F16", { "sketchPlane" : qUnion([Q0])});
            skCircle(sketch, "E79", {"center": v(0, 120) * mm, "radius": 6 * mm});
            skPoint(sketch, "E79.centerSnap0", {"position": v(0, 90) * mm});
            skArc(sketch, "E80", {"start": v(15, 120) * mm, "mid": v(0, 135) * mm, "end": v(-15, 120) * mm});
            skLineSegment(sketch, "E81", {"start": v(-15, 120) * mm, "end": v(-15, 108) * mm});
            skLineSegment(sketch, "E82", {"start": v(-33, 90) * mm, "end": v(-15, 108) * mm});
            skLineSegment(sketch, "E83", {"start": v(15, 108) * mm, "end": v(15, 120) * mm});
            skLineSegment(sketch, "E84", {"start": v(15, 108) * mm, "end": v(33, 90) * mm});
            skLineSegment(sketch, "E85", {"start": v(-80, 0) * mm, "end": v(80, 0) * mm, "construction": true});
            skCircle(sketch, "E86.MirrorC", {"center": v(0, -120) * mm, "radius": 6 * mm});
            skLineSegment(sketch, "E87.MirrorCS", {"start": v(-15, -120) * mm, "end": v(-15, -108) * mm});
            skArc(sketch, "E88.MirrorCS", {"start": v(15, -120) * mm, "mid": v(0, -135) * mm, "end": v(-15, -120) * mm});
            skLineSegment(sketch, "E89.MirrorCS", {"start": v(15, -108) * mm, "end": v(15, -120) * mm});
            skLineSegment(sketch, "E90.MirrorCS", {"start": v(15, -108) * mm, "end": v(33, -90) * mm});
            skLineSegment(sketch, "E91.MirrorCS", {"start": v(-33, -90) * mm, "end": v(-15, -108) * mm});
            skPoint(sketch, "E92.MirrorP", {"position": v(0, -90) * mm});
            skSolve(sketch);
        }
        {
            var Q0;
            Q0=makeQuery(id+"F16.imprint","IMPRINT",FACE,{"disambiguationData":[TD([[makeQuery(id+"F16.imprint","IMPRINT",EDGE,{"derivedFrom":sQuery(id+"F16.wireOp",EDGE,"E79")}),-1.0]])]});
            var Q1;
            {var subQ1=sQuery(id+"F16.wireOp",EDGE,"E90.MirrorCS");Q1=makeQuery(id+"F16.imprint","IMPRINT",FACE,{"disambiguationData":[TD([[makeQuery(id+"F16.imprint","IMPRINT",EDGE,{"derivedFrom":subQ1}),1.0]])]});}
            var Q2;
            Q2=makeQuery(id+"F16.imprint","IMPRINT",FACE,{"disambiguationData":[TD([[makeQuery(id+"F16.imprint","IMPRINT",EDGE,{"derivedFrom":makeQuery(id+"F1.opExtrude","CAP_EDGE",EDGE,{"disambiguationData":[OSD([sQuery(id+"F0.wireOp",EDGE,"E1.left")])],"isStart":true})}),-1.0]])]});
            var Q3;
            Q3=makeQuery(id+"F2.opExtrude","CAP_FACE",FACE,{"disambiguationData":[OSD([sQuery(id+"F0.wireOp",EDGE,"E12"),sQuery(id+"F0.wireOp",EDGE,"E13"),sQuery(id+"F0.wireOp",EDGE,"E14"),sQuery(id+"F0.wireOp",EDGE,"E15"),sQuery(id+"F0.wireOp",EDGE,"E17.filletArc"),sQuery(id+"F0.wireOp",EDGE,"E18.filletArc"),sQuery(id+"F0.wireOp",EDGE,"E19.filletArc"),sQuery(id+"F0.wireOp",EDGE,"E20.filletArc"),sQuery(id+"F0.wireOp",EDGE,"E25.0"),sQuery(id+"F0.wireOp",EDGE,"E25.1"),sQuery(id+"F0.wireOp",EDGE,"E25.2"),sQuery(id+"F0.wireOp",EDGE,"E25.3"),sQuery(id+"F0.wireOp",EDGE,"E25.4"),sQuery(id+"F0.wireOp",EDGE,"E25.5"),sQuery(id+"F0.wireOp",EDGE,"E25.6"),sQuery(id+"F0.wireOp",EDGE,"E25.7")])],"isStart":false});
            extrude(context, id + "F17", {"entities" : qUnion([Q0, Q1, Q2]), "operationType" : NewBodyOperationType.ADD, "endBound" : BoundingType.UP_TO_SURFACE, "depth" : 25 * mm, "endBoundEntityFace" : qUnion([Q3]), "offsetDistance" : 25 * mm});
        }
    });
